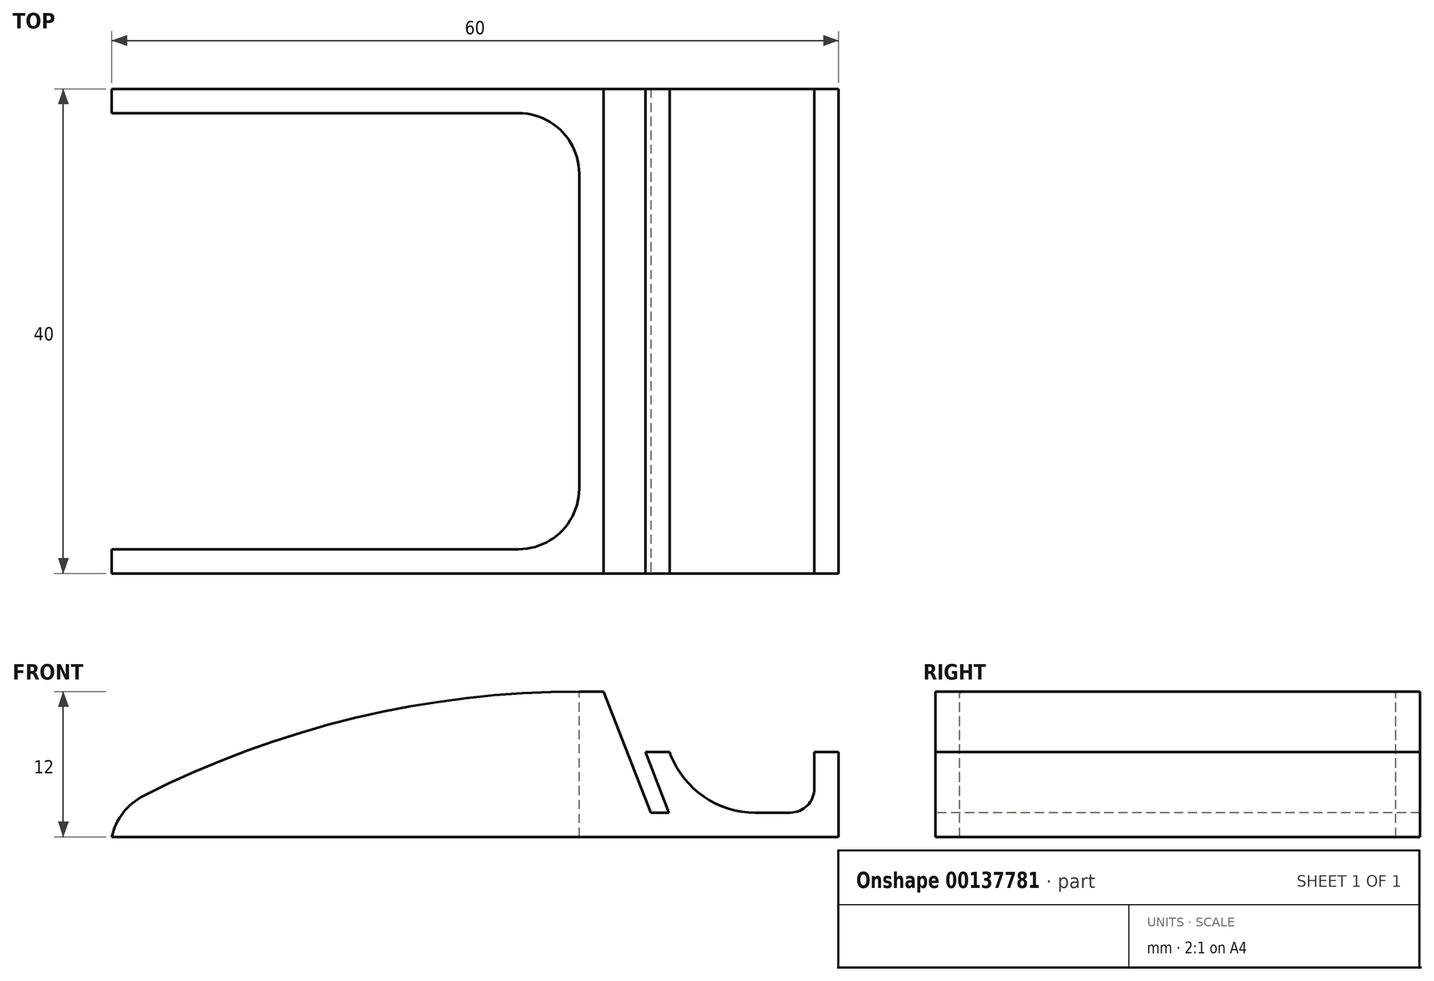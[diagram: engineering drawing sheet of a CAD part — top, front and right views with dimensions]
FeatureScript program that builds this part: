
annotation { "Feature Type Name" : "Feature", "Feature Type Description" : "" }
export const myFeature = defineFeature(function(context is Context, id is Id, definition is map)
    precondition{}
    {
        {
            var Q0;
            Q0=qCreatedBy(makeId("Front.planeOp"),FACE);
            var sketch = newSketch(context, id + "F0", { "sketchPlane" : qUnion([Q0])});
            skLineSegment(sketch, "E0", {"start": v(0, 0) * mm, "end": v(-10, 0) * mm});
            skLineSegment(sketch, "E1", {"start": v(-10, 0) * mm, "end": v(-11.96, 5) * mm});
            skLineSegment(sketch, "E2", {"start": v(-11.96, 5) * mm, "end": v(-13.96, 5) * mm});
            skLineSegment(sketch, "E3", {"start": v(-13.96, 5) * mm, "end": v(-12, 0) * mm});
            skLineSegment(sketch, "E4", {"start": v(-12, 0) * mm, "end": v(-13.5, 0) * mm});
            skLineSegment(sketch, "E5", {"start": v(-13.5, 0) * mm, "end": v(-17.42, 10) * mm});
            skLineSegment(sketch, "E6", {"start": v(-17.42, 10) * mm, "end": v(-19.42, 10) * mm});
            skLineSegment(sketch, "E7", {"start": v(-19.42, 10) * mm, "end": v(-19.42, 0) * mm});
            skLineSegment(sketch, "E8", {"start": v(-19.42, 0) * mm, "end": v(-58, 0) * mm});
            skLineSegment(sketch, "E9", {"start": v(-58, 0) * mm, "end": v(-58, -2) * mm});
            skLineSegment(sketch, "E10", {"start": v(-58, -2) * mm, "end": v(2, -2) * mm});
            skLineSegment(sketch, "E11", {"start": v(2, -2) * mm, "end": v(2, 5) * mm});
            skLineSegment(sketch, "E12", {"start": v(2, 5) * mm, "end": v(0, 5) * mm});
            skLineSegment(sketch, "E13", {"start": v(0, 5) * mm, "end": v(0, 0) * mm});
            skArc(sketch, "E14", {"start": v(-19.42, 10) * mm, "mid": v(-39.35, 7.46) * mm, "end": v(-58, 0) * mm});
            skSolve(sketch);
        }
        {
            var Q0;
            Q0=makeQuery(id+"F0.imprint","IMPRINT",FACE,{"disambiguationData":[TD([[makeQuery(id+"F0.imprint","IMPRINT",EDGE,{"derivedFrom":sQuery(id+"F0.wireOp",EDGE,"E7")}),-1.0]])]});
            var Q1;
            Q1=makeQuery(id+"F0.imprint","IMPRINT",FACE,{"disambiguationData":[TD([[makeQuery(id+"F0.imprint","IMPRINT",EDGE,{"derivedFrom":sQuery(id+"F0.wireOp",EDGE,"E0")}),1.0]])]});
            extrude(context, id + "F1", {"entities" : qUnion([Q0, Q1]), "oppositeDirection" : true, "depth" : 40 * mm});
        }
        {
            var Q0;
            Q0=makeQuery(id+"F1.opExtrude","SWEPT_EDGE",EDGE,{"disambiguationData":[OSD([sQuery(id+"F0.wireOp",EDGE,"E0"),sQuery(id+"F0.wireOp",EDGE,"E1")])]});
            fillet(context, id + "F2", {"entities" : qUnion([Q0]), "radius" : 7.5 * mm, "tangentPropagation" : true, "allowEdgeOverflow" : false});
        }
        {
            var Q0;
            Q0=makeQuery(id+"F1.opExtrude","SWEPT_EDGE",EDGE,{"disambiguationData":[OSD([sQuery(id+"F0.wireOp",EDGE,"E0"),sQuery(id+"F0.wireOp",EDGE,"E13")])]});
            fillet(context, id + "F3", {"entities" : qUnion([Q0]), "radius" : 2 * mm, "tangentPropagation" : true, "allowEdgeOverflow" : false});
        }
        {
            var Q0;
            Q0=makeQuery(id+"F1.opExtrude","SWEPT_FACE",FACE,{"disambiguationData":[OSD([sQuery(id+"F0.wireOp",EDGE,"E6")])]});
            var sketch = newSketch(context, id + "F4", { "sketchPlane" : qUnion([Q0])});
            skLineSegment(sketch, "E15.bottom", {"start": v(-19.42, 2) * mm, "end": v(-58, 2) * mm});
            skLineSegment(sketch, "E15.top", {"start": v(-19.42, 38) * mm, "end": v(-58, 38) * mm});
            skLineSegment(sketch, "E15.left", {"start": v(-19.42, 2) * mm, "end": v(-19.42, 38) * mm});
            skLineSegment(sketch, "E15.right", {"start": v(-58, 2) * mm, "end": v(-58, 38) * mm});
            skSolve(sketch);
        }
        {
            var Q0;
            Q0=makeQuery(id+"F4.imprint","IMPRINT",FACE,{"disambiguationData":[TD([[makeQuery(id+"F4.imprint","IMPRINT",EDGE,{"derivedFrom":sQuery(id+"F4.wireOp",EDGE,"E15.bottom")}),-1.0]])]});
            extrude(context, id + "F5", {"entities" : qUnion([Q0]), "operationType" : NewBodyOperationType.REMOVE, "oppositeDirection" : true, "depth" : 25.4 * mm});
        }
        {
            var Q0;
            Q0=makeQuery(id+"F5.boolean.opBoolean","COPY",EDGE,{"derivedFrom":makeQuery(id+"F5.opExtrude","SWEPT_EDGE",EDGE,{"disambiguationData":[OSD([sQuery(id+"F0.wireOp",EDGE,"E6"),sQuery(id+"F0.wireOp",EDGE,"E7"),sQuery(id+"F0.wireOp",EDGE,"E14"),sQuery(id+"F4.wireOp",EDGE,"E15.bottom"),sQuery(id+"F4.wireOp",EDGE,"E15.left")])]})});
            var Q1;
            Q1=makeQuery(id+"F5.boolean.opBoolean","COPY",EDGE,{"derivedFrom":makeQuery(id+"F5.opExtrude","SWEPT_EDGE",EDGE,{"disambiguationData":[OSD([sQuery(id+"F0.wireOp",EDGE,"E6"),sQuery(id+"F0.wireOp",EDGE,"E7"),sQuery(id+"F0.wireOp",EDGE,"E14"),sQuery(id+"F4.wireOp",EDGE,"E15.top"),sQuery(id+"F4.wireOp",EDGE,"E15.left")])]})});
            fillet(context, id + "F6", {"entities" : qUnion([Q0, Q1]), "radius" : 5 * mm, "tangentPropagation" : true, "allowEdgeOverflow" : false});
        }
        {
            var Q0;
            {var subQ0=sQuery(id+"F0.wireOp",EDGE,"E14");var subQ1=sQuery(id+"F0.wireOp",EDGE,"E9");Q0=makeQuery(id+"F5.boolean.opBoolean","SPLIT",EDGE,{"disambiguationData":[TD([makeQuery(id+"F5.opExtrude","SWEPT_FACE",FACE,{"disambiguationData":[OSD([sQuery(id+"F4.wireOp",EDGE,"E15.bottom")])]})])],"derivedFrom":makeQuery(id+"F1.opExtrude","SWEPT_EDGE",EDGE,{"disambiguationData":[OSD([sQuery(id+"F0.wireOp",EDGE,"E8"),subQ1,subQ0])]})});}
            var Q1;
            {var subQ0=sQuery(id+"F0.wireOp",EDGE,"E14");var subQ1=sQuery(id+"F0.wireOp",EDGE,"E9");Q1=makeQuery(id+"F5.boolean.opBoolean","SPLIT",EDGE,{"disambiguationData":[TD([makeQuery(id+"F5.opExtrude","SWEPT_FACE",FACE,{"disambiguationData":[OSD([sQuery(id+"F4.wireOp",EDGE,"E15.top")])]})])],"derivedFrom":makeQuery(id+"F1.opExtrude","SWEPT_EDGE",EDGE,{"disambiguationData":[OSD([sQuery(id+"F0.wireOp",EDGE,"E8"),subQ1,subQ0])]})});}
            fillet(context, id + "F7", {"entities" : qUnion([Q0, Q1]), "radius" : 5 * mm, "tangentPropagation" : true, "allowEdgeOverflow" : false});
        }
    });
